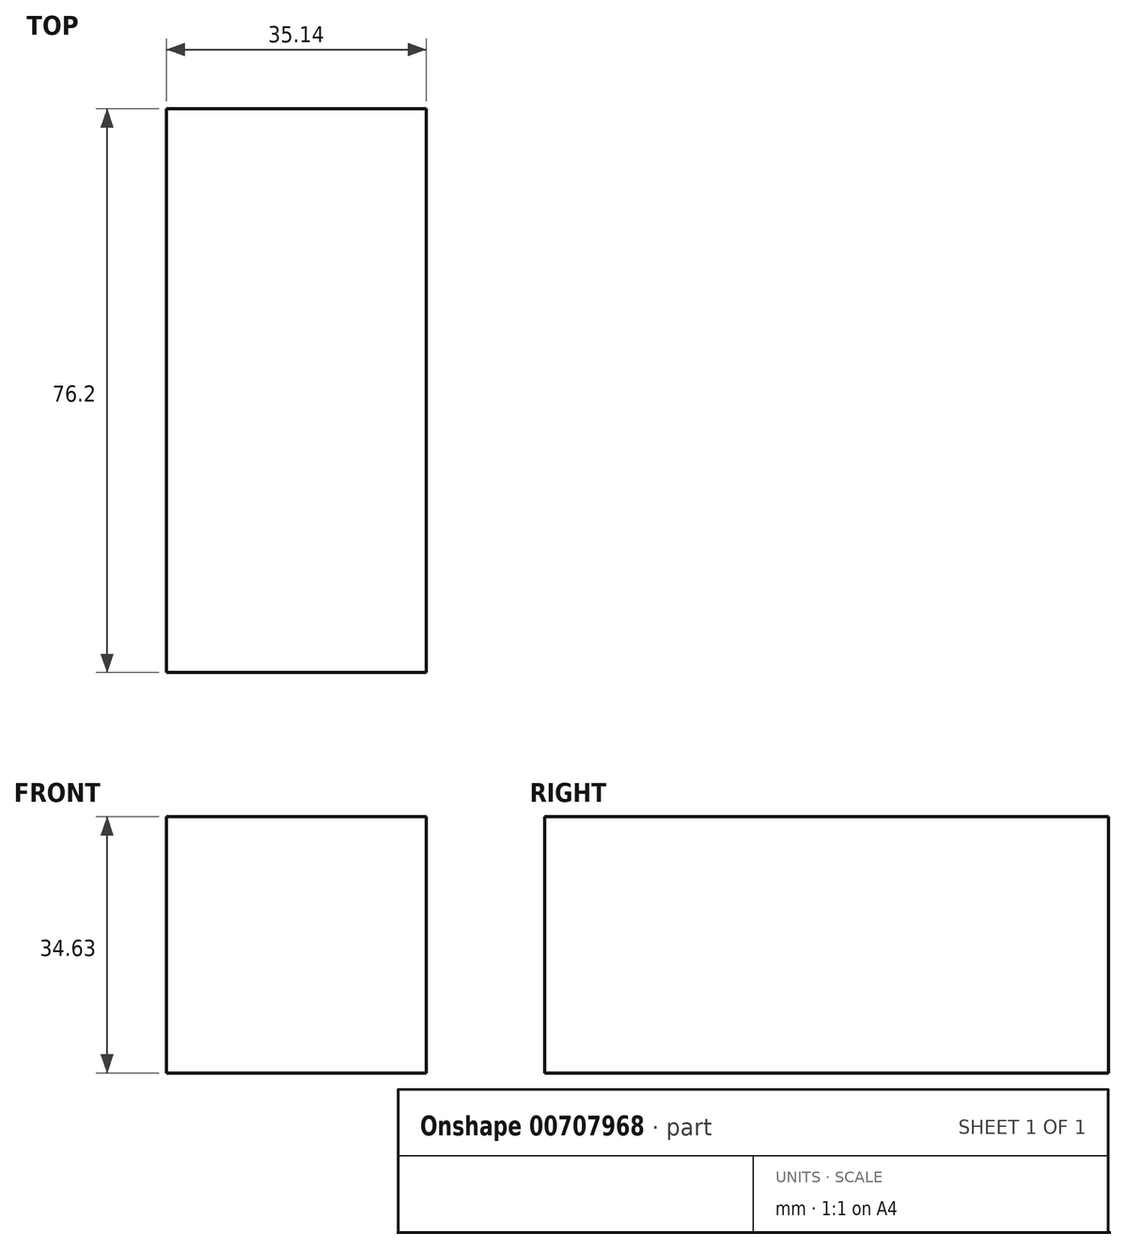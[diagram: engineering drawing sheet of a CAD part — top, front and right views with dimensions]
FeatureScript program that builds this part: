
annotation { "Feature Type Name" : "Feature", "Feature Type Description" : "" }
export const myFeature = defineFeature(function(context is Context, id is Id, definition is map)
    precondition{}
    {
        {
            var Q0;
            Q0=qCreatedBy(makeId("Front.planeOp"),FACE);
            var sketch = newSketch(context, id + "F0", { "sketchPlane" : qUnion([Q0])});
            skLineSegment(sketch, "E0.bottom", {"start": v(0, 0) * mm, "end": v(35.14, 0) * mm});
            skLineSegment(sketch, "E0.top", {"start": v(0, 34.63) * mm, "end": v(35.14, 34.63) * mm});
            skLineSegment(sketch, "E0.left", {"start": v(0, 0) * mm, "end": v(0, 34.63) * mm});
            skLineSegment(sketch, "E0.right", {"start": v(35.14, 0) * mm, "end": v(35.14, 34.63) * mm});
            skSolve(sketch);
        }
        {
            var Q0;
            Q0=makeQuery(id+"F0.imprint","IMPRINT",FACE,{"disambiguationData":[TD([[makeQuery(id+"F0.imprint","IMPRINT",EDGE,{"derivedFrom":sQuery(id+"F0.wireOp",EDGE,"E0.bottom")}),1.0]])]});
            extrude(context, id + "F1", {"entities" : qUnion([Q0]), "depth" : 76.2 * mm, "offsetDistance" : 25.4 * mm});
        }
    });
